# Revit family: IS_Eurovit_V3403_BIM_DE
name_source: partatom
category: Plumbing Fixtures
revit_build: Autodesk Revit MEP 2016 (Build: 20161004_0715(x64)
units: mm (PartAtom-declared; Revit-internal decimal feet)

## family parameters
Always vertical = No
Cut with Voids When Loaded = No
OmniClass Number = 23.45.05.21.11.11
OmniClass Title = Water Operated Water Closets
Part Type = Normal
Room Calculation Point = No
Round Connector Dimension = Use Diameter
Shared = No
Work Plane-Based = No

## types (1)
- V340301 - EUROVIT wall mounted bowl 355x520mm, washout
    Accessories = www.idealstandard.de\ersatzteile
    AssetType = Fixed
    BIMObjectName = ISI_IdealStandard_WcPans_Eurovit_V340301
    BIMobject category = Toilets
    BOSUseNativeGeometries = 1
    BarCode = 8595095902640
    Brand = Ideal Standard
    Brand url = http://www.idealstandard.de
    CodePerformance = DIN EN 997 CL1-6A, DIN EN 33
    Color = White
    ConnectionType = Plumbing
    Cost = 0 $
    CurrencyUnit = €
    CurrentRevision = 1
    Date of publishing = 20/12/2017
    Description = IS Wandflachspülklosett EUROVIT, 355x520x370mm, Weiß
    DurationUnit = Year
    EAN code = https://8595095902640
    Edition number = 1
    ExpectedLife = 25
    Features = IS Wandflachspülklosett EUROVIT, 355x520x370mm, Weiß
    Finish = White
    IFC Classification = Sanitary Terminal
    IfcExportAs = IfcSanitaryTerminalType
    Installation instructions = http://www.idealstandard.de
    InstallationInstructions = www.idealstandard.de\produkte
    MainColor = White
    MaintenanceInformation = www.idealstandard.de\produkte
    Manufacturer name = Ideal Standard
    ManufacturerURL = http://www.idealstandard.de
    Material = Vitreous china
    Material main = Ceramics
    Model = V340301
    ModelNumber = V340301
    ModelReference = IS Wandflachspülklosett EUROVIT, 355x520x370mm, Weiß
    NBS Reference Code = 35-93-94
    NBS Reference Description = Wc Pans
    Name = WcPans_Eurovit_V340301
    NettWeight = 18 Kg
    Nominal height = 370
    Nominal width = 355
    NominalDepth = 520 mm  [stored 1.70604 ft]
    NominalHeight = 371 mm
    NominalLength = 520 mm  [stored 1.70604 ft]
    NominalWidth = 356 mm
    OmniClass Code = 23-31 19 00
    OmniClass Description = Toilets
    OutletConnectionSize = 0 mm  [stored 0 ft]
    PanMaterial = Ceramic
    Product Guid = cf2f0355-31b2-4b2b-bf97-d6e0adf0bd20
    Product SKU = V3403
    Product data url = https://bimobject.com
    Product family = Sanitary
    Product group = Bowl
    Product name = EUROVIT wall mounted bowl 355x520mm, washout
    Product url = http://www.idealstandard.de
    ProductInformation = www.idealstandard.de/produkte
    QR code = http://bimobject.com
    Shape = Sculptured
    Size = 371 x 520 x 356mm
    Space = Internal
    SpareParts = www.idealstandard.de/ersatzteile
    SpilloverLevel = 0 mm  [stored 0 ft]
    Technical description = http://www.idealstandard.de
    ToiletType = Washdown
    URL = http://www.idealstandard.de
    Uniclass2015Code = Pr_40_20_93_94
    Uniclass2015Title = WC pans
    Uniclass2015Version = Products v1.1
    Version = 1
    VolumeUnits = Litres
    Weight Net (Kg) = 18

note: [stored X ft] marks values corroborated as IEEE doubles in the binary element streams (Revit-internal decimal feet)

## geometry (parser evidence)
native form markers: Blend x4, Sweep x1
no freeform markers — native parametric forms only
